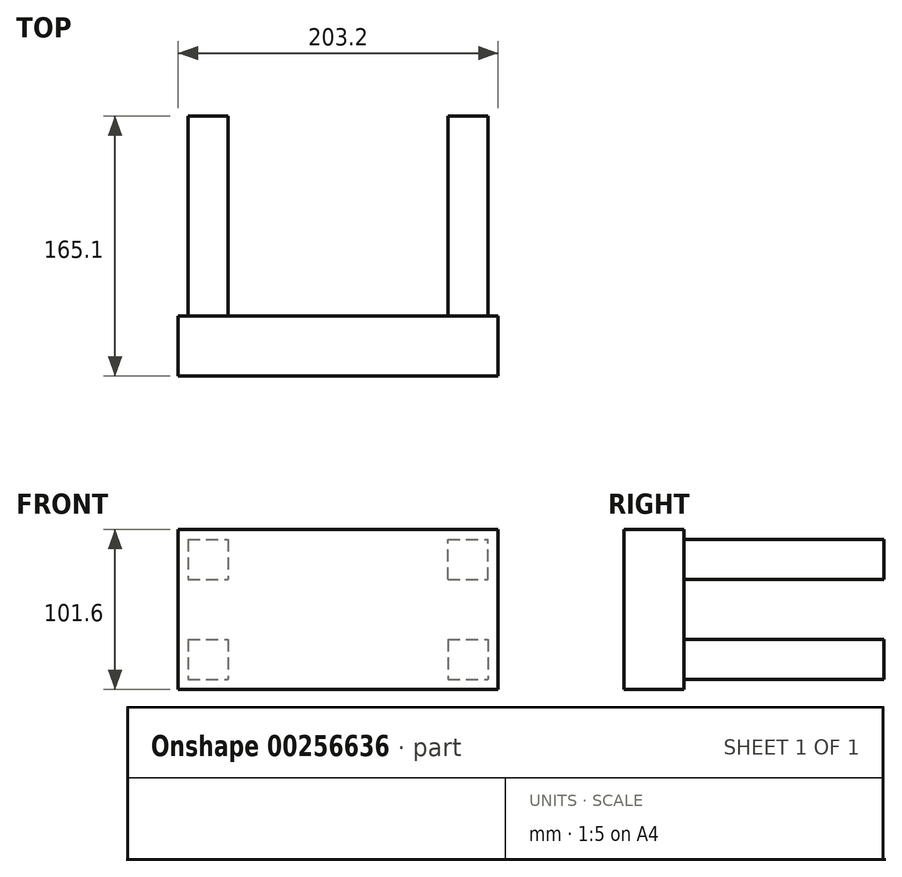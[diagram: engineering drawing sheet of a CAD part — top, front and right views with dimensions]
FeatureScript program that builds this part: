
annotation { "Feature Type Name" : "Feature", "Feature Type Description" : "" }
export const myFeature = defineFeature(function(context is Context, id is Id, definition is map)
    precondition{}
    {
        {
            var Q0;
            Q0=qCreatedBy(makeId("Front.planeOp"),FACE);
            var sketch = newSketch(context, id + "F0", { "sketchPlane" : qUnion([Q0])});
            skLineSegment(sketch, "E0.bottom", {"start": v(-103.96, -54.62) * mm, "end": v(99.24, -54.62) * mm});
            skLineSegment(sketch, "E0.top", {"start": v(-103.96, 46.98) * mm, "end": v(99.24, 46.98) * mm});
            skLineSegment(sketch, "E0.left", {"start": v(-103.96, -54.62) * mm, "end": v(-103.96, 46.98) * mm});
            skLineSegment(sketch, "E0.right", {"start": v(99.24, -54.62) * mm, "end": v(99.24, 46.98) * mm});
            skLineSegment(sketch, "E1.bottom", {"start": v(-97.61, 40.63) * mm, "end": v(-72.21, 40.63) * mm});
            skLineSegment(sketch, "E1.top", {"start": v(-97.61, 15.23) * mm, "end": v(-72.21, 15.23) * mm});
            skLineSegment(sketch, "E1.left", {"start": v(-97.61, 40.63) * mm, "end": v(-97.61, 15.23) * mm});
            skLineSegment(sketch, "E1.right", {"start": v(-72.21, 40.63) * mm, "end": v(-72.21, 15.23) * mm});
            skPoint(sketch, "E1.middle", {"position": v(-84.91, 27.93) * mm});
            skLineSegment(sketch, "E2.bottom", {"start": v(-97.61, -22.87) * mm, "end": v(-72.21, -22.87) * mm});
            skLineSegment(sketch, "E2.top", {"start": v(-97.61, -48.27) * mm, "end": v(-72.21, -48.27) * mm});
            skLineSegment(sketch, "E2.left", {"start": v(-97.61, -22.87) * mm, "end": v(-97.61, -48.27) * mm});
            skLineSegment(sketch, "E2.right", {"start": v(-72.21, -22.87) * mm, "end": v(-72.21, -48.27) * mm});
            skPoint(sketch, "E2.middle", {"position": v(-84.91, -35.57) * mm});
            skPoint(sketch, "E2.middle.positionSnap0", {"position": v(-84.91, 15.23) * mm});
            skPoint(sketch, "E2.centerSnap0", {"position": v(-84.91, 15.23) * mm});
            skLineSegment(sketch, "E3.bottom", {"start": v(67.49, -22.87) * mm, "end": v(92.89, -22.87) * mm});
            skLineSegment(sketch, "E3.top", {"start": v(67.49, -48.27) * mm, "end": v(92.89, -48.27) * mm});
            skLineSegment(sketch, "E3.left", {"start": v(67.49, -22.87) * mm, "end": v(67.49, -48.27) * mm});
            skLineSegment(sketch, "E3.right", {"start": v(92.89, -22.87) * mm, "end": v(92.89, -48.27) * mm});
            skPoint(sketch, "E3.middle", {"position": v(80.19, -35.57) * mm});
            skPoint(sketch, "E3.middle.positionSnap0", {"position": v(-72.21, -35.57) * mm});
            skPoint(sketch, "E3.centerSnap0", {"position": v(-72.21, -35.57) * mm});
            skLineSegment(sketch, "E4.bottom", {"start": v(67.49, 15.23) * mm, "end": v(92.89, 15.23) * mm});
            skLineSegment(sketch, "E4.top", {"start": v(67.49, 40.63) * mm, "end": v(92.89, 40.63) * mm});
            skLineSegment(sketch, "E4.left", {"start": v(67.49, 15.23) * mm, "end": v(67.49, 40.63) * mm});
            skLineSegment(sketch, "E4.right", {"start": v(92.89, 15.23) * mm, "end": v(92.89, 40.63) * mm});
            skPoint(sketch, "E4.middle", {"position": v(80.19, 27.93) * mm});
            skPoint(sketch, "E4.middle.positionSnap0", {"position": v(80.19, -22.87) * mm});
            skPoint(sketch, "E4.centerSnap0", {"position": v(80.19, -22.87) * mm});
            skSolve(sketch);
        }
        {
            var Q0;
            Q0 = qSketchRegion(id + "F0", true);
            var Q1;
            Q1=makeQuery(id+"F0.imprint","IMPRINT",FACE,{"disambiguationData":[TD([[makeQuery(id+"F0.imprint","IMPRINT",EDGE,{"derivedFrom":sQuery(id+"F0.wireOp",EDGE,"E2.bottom")}),-1.0]])]});
            var Q2;
            Q2=makeQuery(id+"F0.imprint","IMPRINT",FACE,{"disambiguationData":[TD([[makeQuery(id+"F0.imprint","IMPRINT",EDGE,{"derivedFrom":sQuery(id+"F0.wireOp",EDGE,"E1.bottom")}),-1.0]])]});
            var Q3;
            Q3=makeQuery(id+"F0.imprint","IMPRINT",FACE,{"disambiguationData":[TD([[makeQuery(id+"F0.imprint","IMPRINT",EDGE,{"derivedFrom":sQuery(id+"F0.wireOp",EDGE,"E4.bottom")}),1.0]])]});
            var Q4;
            Q4=makeQuery(id+"F0.imprint","IMPRINT",FACE,{"disambiguationData":[TD([[makeQuery(id+"F0.imprint","IMPRINT",EDGE,{"derivedFrom":sQuery(id+"F0.wireOp",EDGE,"E3.bottom")}),-1.0]])]});
            extrude(context, id + "F1", {"entities" : qUnion([Q0, Q1, Q2, Q3, Q4]), "depth" : 38.1 * mm});
        }
        {
            var Q0;
            Q0=makeQuery(id+"F0.imprint","IMPRINT",FACE,{"disambiguationData":[TD([[makeQuery(id+"F0.imprint","IMPRINT",EDGE,{"derivedFrom":sQuery(id+"F0.wireOp",EDGE,"E2.bottom")}),-1.0]])]});
            var Q1;
            Q1=makeQuery(id+"F0.imprint","IMPRINT",FACE,{"disambiguationData":[TD([[makeQuery(id+"F0.imprint","IMPRINT",EDGE,{"derivedFrom":sQuery(id+"F0.wireOp",EDGE,"E1.bottom")}),-1.0]])]});
            var Q2;
            Q2=makeQuery(id+"F0.imprint","IMPRINT",FACE,{"disambiguationData":[TD([[makeQuery(id+"F0.imprint","IMPRINT",EDGE,{"derivedFrom":sQuery(id+"F0.wireOp",EDGE,"E4.bottom")}),1.0]])]});
            var Q3;
            Q3=makeQuery(id+"F0.imprint","IMPRINT",FACE,{"disambiguationData":[TD([[makeQuery(id+"F0.imprint","IMPRINT",EDGE,{"derivedFrom":sQuery(id+"F0.wireOp",EDGE,"E3.bottom")}),-1.0]])]});
            extrude(context, id + "F2", {"entities" : qUnion([Q0, Q1, Q2, Q3]), "oppositeDirection" : true, "depth" : 127 * mm});
        }
    });
